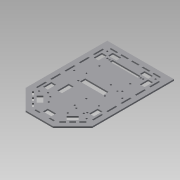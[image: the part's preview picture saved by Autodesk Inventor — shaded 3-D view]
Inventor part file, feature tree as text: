
AUTODESK INVENTOR PART (.ipt)
format: ipt  version: 2015 SP1 (Build 190203100, 203)  size: 326,144 bytes
history: native  units: mm
features: extrude x1, sketch x1
ambient origin geometry x8: Origin, YZ Plane, XZ Plane, XY Plane, X Axis, Y Axis, Z Axis, Center Point
bodies: Body1 (feature_tree)
feature tree (2):
  extrude  "Extrusion2"  Depth=3.0mm
  sketch  "Sketch1"  dims[d0=10.0mm d1=3.0mm d2=20.0mm d4=15.0mm d5=20.0mm d7=15.0mm d10=1.5mm d11=10.0mm d12=3.0mm d13=10.0mm d14=135.0deg d15=45.0deg d16=20.0mm d18=15.0mm d19=20.0mm d21=15.0mm d24=3.0mm d25=20.0mm d26=30.0mm d28=30.0mm d29=30.0mm d31=30.0mm d34=15.0mm d35=3.0mm d36=30.0mm d38=22.5mm d39=30.0mm d41=22.5mm d47=3.0mm d48=0.0mm d49=76.821555mm]
